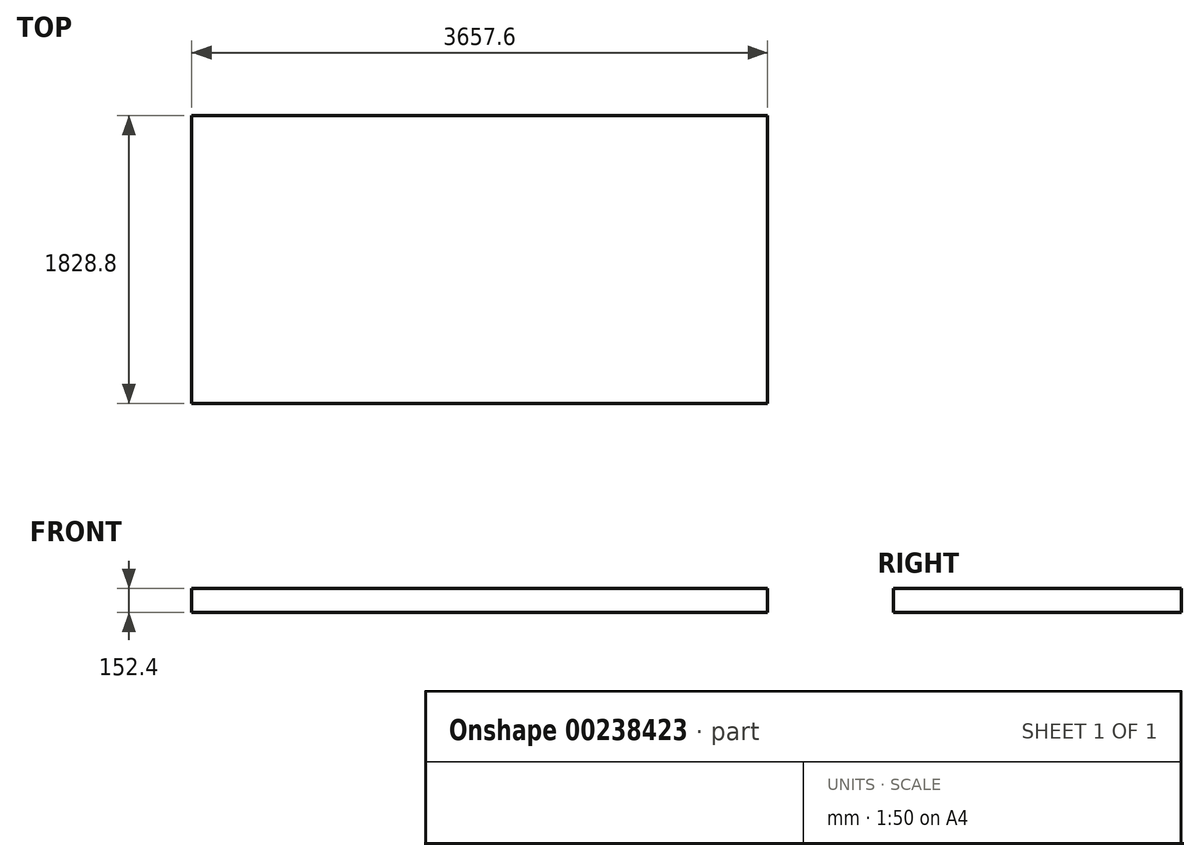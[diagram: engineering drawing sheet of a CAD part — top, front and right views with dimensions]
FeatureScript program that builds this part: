
annotation { "Feature Type Name" : "Feature", "Feature Type Description" : "" }
export const myFeature = defineFeature(function(context is Context, id is Id, definition is map)
    precondition{}
    {
        {
            var Q0;
            Q0=qCreatedBy(makeId("Top.planeOp"),FACE);
            var sketch = newSketch(context, id + "F0", { "sketchPlane" : qUnion([Q0])});
            skLineSegment(sketch, "E0.bottom", {"start": v(-67.06, 1820.76) * mm, "end": v(3590.54, 1820.76) * mm});
            skLineSegment(sketch, "E0.top", {"start": v(-67.06, -8.04) * mm, "end": v(3590.54, -8.04) * mm});
            skLineSegment(sketch, "E0.left", {"start": v(-67.06, 1820.76) * mm, "end": v(-67.06, -8.04) * mm});
            skLineSegment(sketch, "E0.right", {"start": v(3590.54, 1820.76) * mm, "end": v(3590.54, -8.04) * mm});
            skSolve(sketch);
        }
        {
            var Q0;
            Q0=makeQuery(id+"F0.imprint","IMPRINT",FACE,{"disambiguationData":[TD([[makeQuery(id+"F0.imprint","IMPRINT",EDGE,{"derivedFrom":sQuery(id+"F0.wireOp",EDGE,"E0.bottom")}),-1.0]])]});
            extrude(context, id + "F1", {"entities" : qUnion([Q0]), "depth" : 152.4 * mm});
        }
    });
